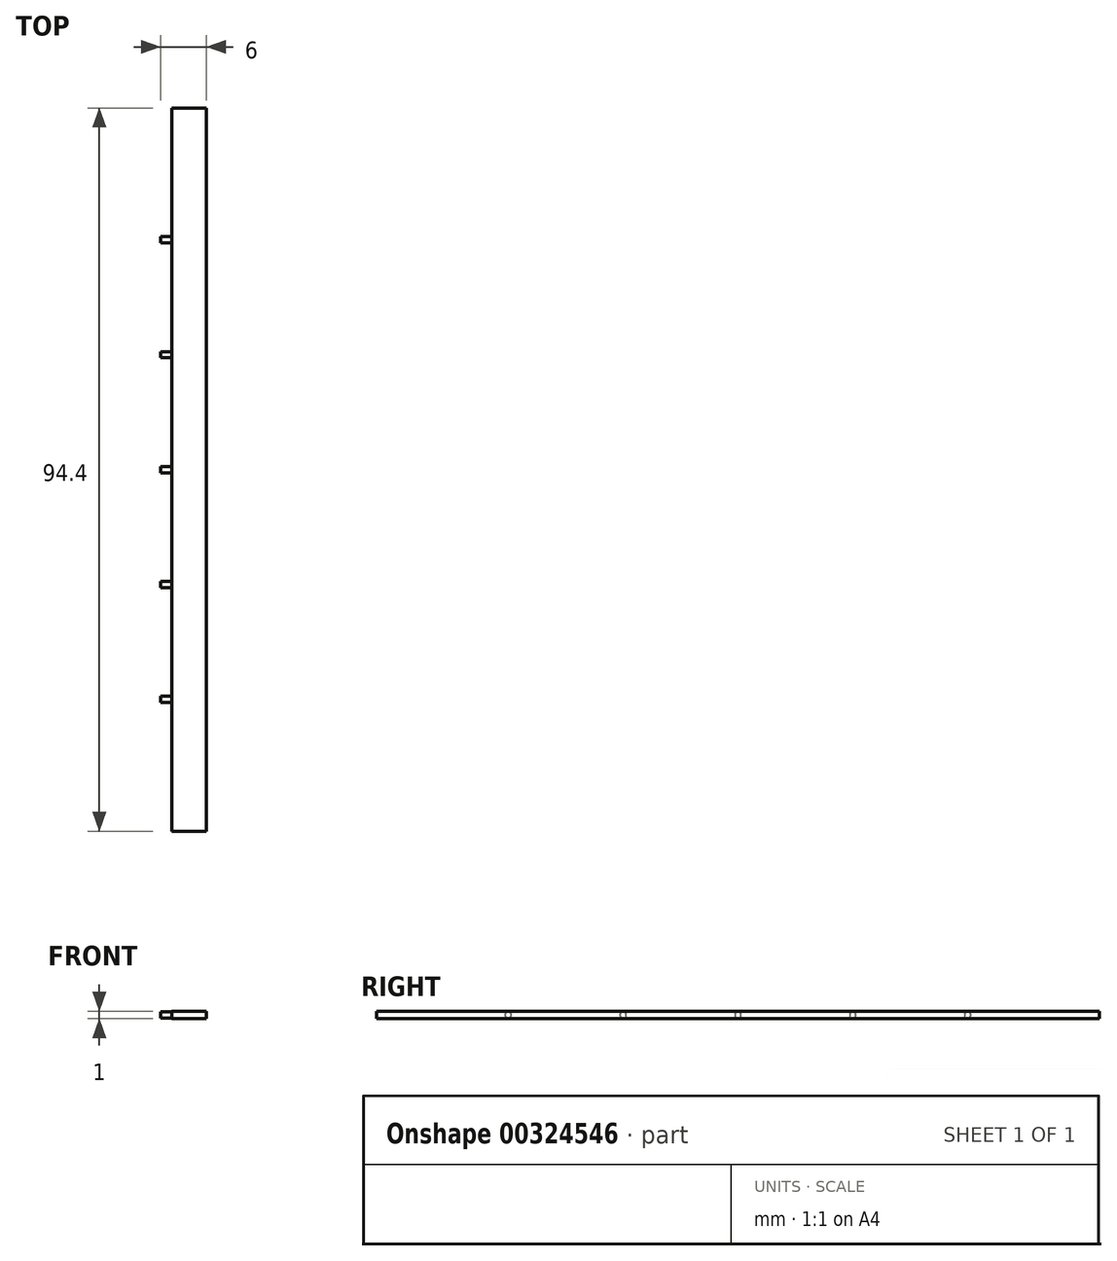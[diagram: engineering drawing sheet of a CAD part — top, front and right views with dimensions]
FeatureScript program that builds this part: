
annotation { "Feature Type Name" : "Feature", "Feature Type Description" : "" }
export const myFeature = defineFeature(function(context is Context, id is Id, definition is map)
    precondition{}
    {
        {
            var Q0;
            Q0=qCreatedBy(makeId("Top.planeOp"),FACE);
            var sketch = newSketch(context, id + "F0", { "sketchPlane" : qUnion([Q0])});
            skLineSegment(sketch, "E0.bottom", {"start": v(-49.64, 77.6) * mm, "end": v(-45.14, 77.6) * mm});
            skLineSegment(sketch, "E0.top", {"start": v(-49.64, -16.8) * mm, "end": v(-45.14, -16.8) * mm});
            skLineSegment(sketch, "E0.left", {"start": v(-49.64, 77.6) * mm, "end": v(-49.64, -16.8) * mm});
            skLineSegment(sketch, "E0.right", {"start": v(-45.14, 77.6) * mm, "end": v(-45.14, -16.8) * mm});
            skSolve(sketch);
        }
        {
            var Q0;
            Q0 = qSketchRegion(id + "F0", true);
            extrude(context, id + "F1", {"entities" : qUnion([Q0]), "oppositeDirection" : true, "depth" : 1 * mm});
        }
        {
            var Q0;
            Q0=makeQuery(id+"F1.opExtrude","SWEPT_FACE",FACE,{"disambiguationData":[OSD([sQuery(id+"F0.wireOp",EDGE,"E0.left")])]});
            var sketch = newSketch(context, id + "F2", { "sketchPlane" : qUnion([Q0])});
            skCircle(sketch, "E1", {"center": v(-30.4, -0.5) * mm, "radius": 0.4 * mm});
            skPoint(sketch, "E1.centerSnap0", {"position": v(-30.4, -1) * mm});
            skCircle(sketch, "E2", {"center": v(-0.4, -0.5) * mm, "radius": 0.4 * mm});
            skCircle(sketch, "E3", {"center": v(-60.4, -0.5) * mm, "radius": 0.4 * mm});
            skCircle(sketch, "E4", {"center": v(-45.4, -0.5) * mm, "radius": 0.4 * mm});
            skCircle(sketch, "E5", {"center": v(-15.4, -0.5) * mm, "radius": 0.4 * mm});
            skSolve(sketch);
        }
        {
            var Q0;
            Q0 = qSketchRegion(id + "F2", true);
            extrude(context, id + "F3", {"entities" : qUnion([Q0]), "operationType" : NewBodyOperationType.ADD, "depth" : 1.5 * mm});
        }
    });
